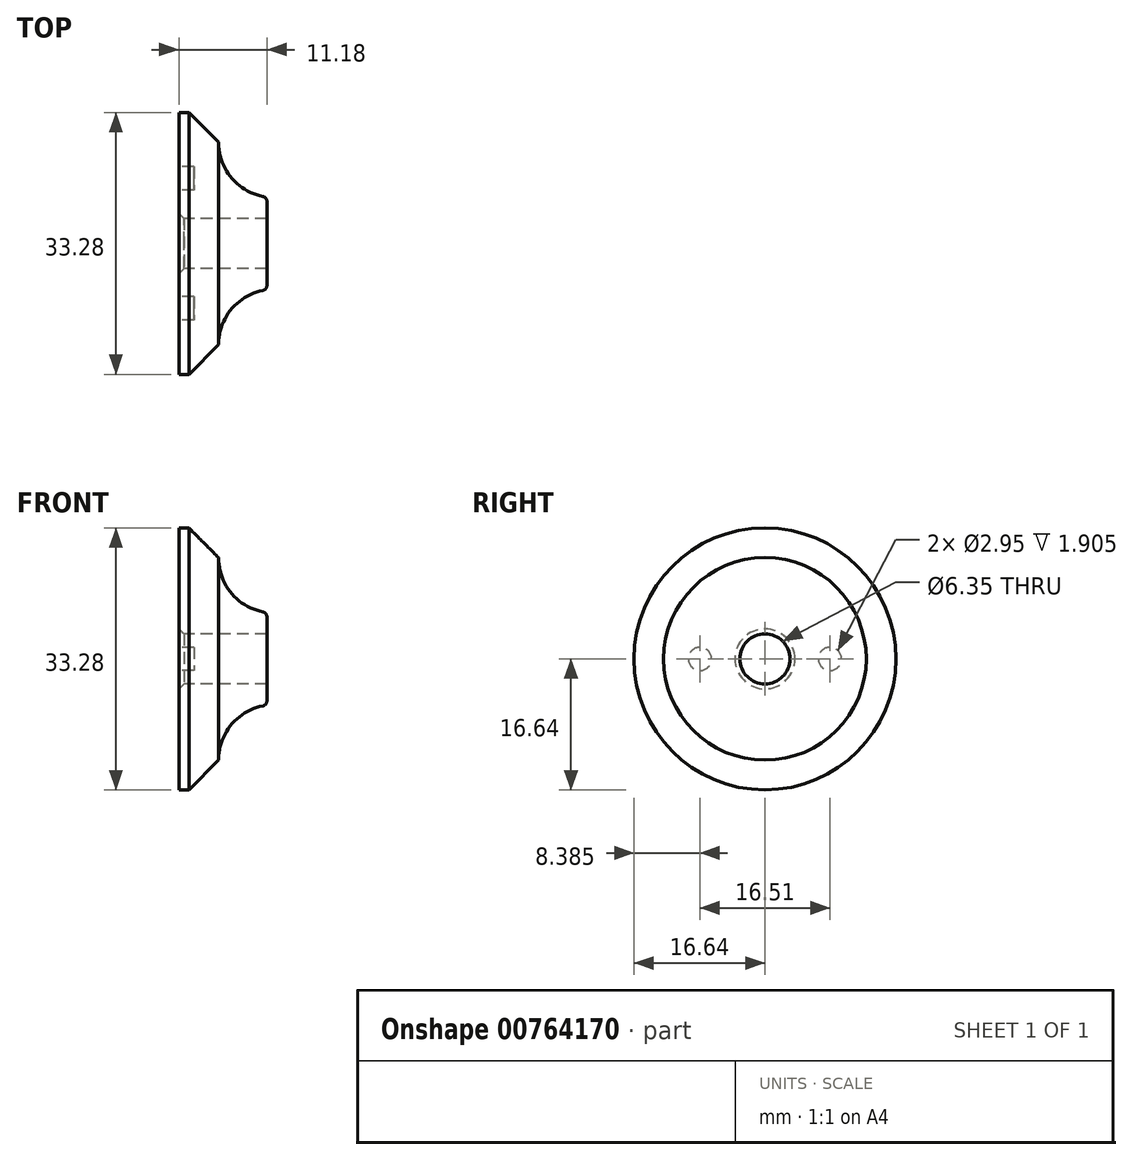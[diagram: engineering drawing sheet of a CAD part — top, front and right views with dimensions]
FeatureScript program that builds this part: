
annotation { "Feature Type Name" : "Feature", "Feature Type Description" : "" }
export const myFeature = defineFeature(function(context is Context, id is Id, definition is map)
    precondition{}
    {
        {
            var Q0;
            Q0=qCreatedBy(makeId("Front.planeOp"),FACE);
            var sketch = newSketch(context, id + "F0", { "sketchPlane" : qUnion([Q0])});
            skLineSegment(sketch, "E0", {"start": v(-1.27, 0) * mm, "end": v(-1.27, 16.64) * mm});
            skLineSegment(sketch, "E1", {"start": v(-1.27, 16.64) * mm, "end": v(0, 16.64) * mm});
            skLineSegment(sketch, "E2", {"start": v(0, 16.64) * mm, "end": v(3.77, 12.87) * mm});
            skLineSegment(sketch, "E3", {"start": v(-1.27, 0) * mm, "end": v(9.9, 0) * mm});
            skLineSegment(sketch, "E4", {"start": v(9.9, 0) * mm, "end": v(9.9, 5.35) * mm});
            skArc(sketch, "E5", {"start": v(3.77, 12.87) * mm, "mid": v(5.34, 8.4) * mm, "end": v(9.4, 5.97) * mm});
            skPoint(sketch, "E6.visualSharp", {"position": v(9.9, 5.9) * mm});
            skArc(sketch, "E6.filletArc", {"start": v(9.9, 5.35) * mm, "mid": v(9.76, 5.75) * mm, "end": v(9.4, 5.97) * mm});
            skSolve(sketch);
        }
        {
            var Q0;
            Q0=makeQuery(id+"F0.imprint","IMPRINT",FACE,{"disambiguationData":[TD([[makeQuery(id+"F0.imprint","IMPRINT",EDGE,{"derivedFrom":sQuery(id+"F0.wireOp",EDGE,"E0")}),-1.0]])]});
            var Q1;
            Q1=sQuery(id+"F0.wireOp",EDGE,"E3");
            revolve(context, id + "F1", {"entities" : qUnion([Q0]), "axis" : qUnion([Q1]), "revolveType" : RevolveType.FULL});
        }
        {
            var Q0;
            Q0=makeQuery(id+"F1.opRevolve","SWEPT_FACE",FACE,{"disambiguationData":[OSD([sQuery(id+"F0.wireOp",EDGE,"E4")])]});
            var sketch = newSketch(context, id + "F2", { "sketchPlane" : qUnion([Q0])});
            skCircle(sketch, "E7", {"center": v(0, 0) * mm, "radius": 3.17 * mm});
            skSolve(sketch);
        }
        {
            var Q0;
            Q0=makeQuery(id+"F1.opRevolve","SWEPT_FACE",FACE,{"disambiguationData":[OSD([sQuery(id+"F0.wireOp",EDGE,"E0")])]});
            var sketch = newSketch(context, id + "F3", { "sketchPlane" : qUnion([Q0])});
            skCircle(sketch, "E8", {"center": v(0, 0) * mm, "radius": 3.18 * mm});
            skSolve(sketch);
        }
        {
            var Q0;
            Q0=makeQuery(id+"F3.imprint","IMPRINT",FACE,{"disambiguationData":[TD([[makeQuery(id+"F3.imprint","IMPRINT",EDGE,{"derivedFrom":sQuery(id+"F3.wireOp",EDGE,"E8")}),1.0]])]});
            extrude(context, id + "F4", {"entities" : qUnion([Q0]), "operationType" : NewBodyOperationType.REMOVE, "oppositeDirection" : true, "depth" : 25.4 * mm});
        }
        {
            var Q0;
            Q0=makeQuery(id+"F3.imprint","IMPRINT",FACE,{"disambiguationData":[TD([[makeQuery(id+"F3.imprint","IMPRINT",EDGE,{"derivedFrom":sQuery(id+"F3.wireOp",EDGE,"E8")}),-1.0]])]});
            var sketch = newSketch(context, id + "F5", { "sketchPlane" : qUnion([Q0])});
            skCircle(sketch, "E9", {"center": v(0, 0) * mm, "radius": 3.81 * mm});
            skSolve(sketch);
        }
        {
            var Q0;
            Q0=qSketchRegion(id+"F5",true);
            extrude(context, id + "F6", {"entities" : qUnion([Q0]), "operationType" : NewBodyOperationType.REMOVE, "oppositeDirection" : true, "depth" : 25.4 * mm, "hasDraft" : true, "draftAngle" : 45 * degree, "draftPullDirection" : true});
        }
        {
            var Q0;
            Q0=makeQuery(id+"F3.imprint","IMPRINT",FACE,{"disambiguationData":[TD([[makeQuery(id+"F3.imprint","IMPRINT",EDGE,{"derivedFrom":sQuery(id+"F3.wireOp",EDGE,"E8")}),-1.0]])]});
            var sketch = newSketch(context, id + "F7", { "sketchPlane" : qUnion([Q0])});
            skPoint(sketch, "E10.0", {"position": v(0, 0) * mm});
            skCircle(sketch, "E11", {"center": v(-8.26, 0) * mm, "radius": 1.47 * mm});
            skCircle(sketch, "E12.MirrorC", {"center": v(8.26, 0) * mm, "radius": 1.47 * mm});
            skSolve(sketch);
        }
        {
            var Q0;
            Q0=qSketchRegion(id+"F7",true);
            var Q1;
            Q1=sQuery(id+"F7.wireOp",EDGE,"E11");
            var Q2;
            Q2=sQuery(id+"F7.wireOp",EDGE,"E12.MirrorC");
            extrude(context, id + "F8", {"entities" : qUnion([Q0]), "operationType" : NewBodyOperationType.REMOVE, "surfaceEntities" : qUnion([Q1, Q2]), "oppositeDirection" : true, "depth" : 1.9 * mm});
        }
    });
